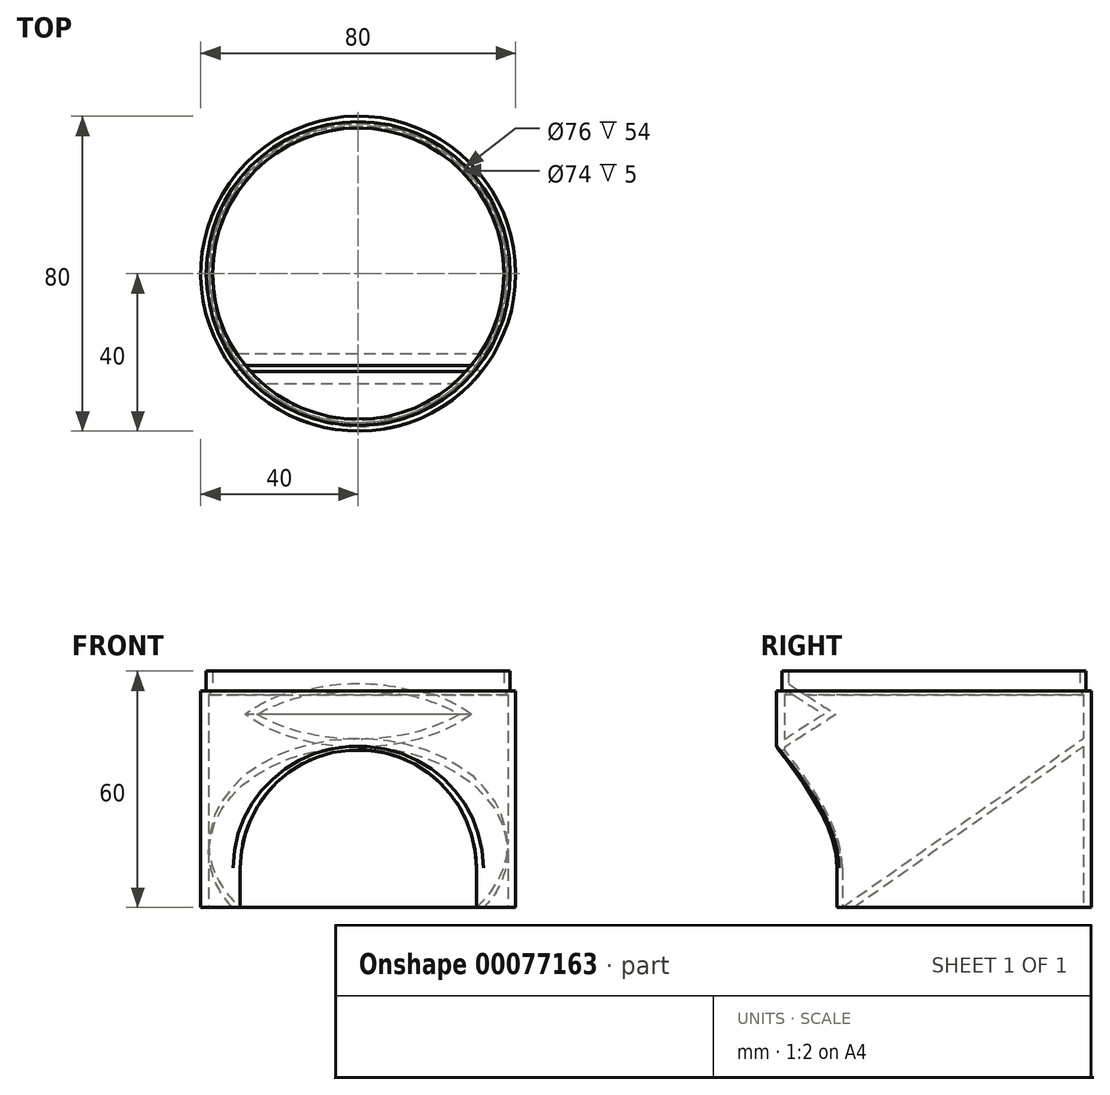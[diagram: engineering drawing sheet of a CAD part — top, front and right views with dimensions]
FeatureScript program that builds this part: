
annotation { "Feature Type Name" : "Feature", "Feature Type Description" : "" }
export const myFeature = defineFeature(function(context is Context, id is Id, definition is map)
    precondition{}
    {
        {
            var Q0;
            Q0=qCreatedBy(makeId("Top.planeOp"),FACE);
            var sketch = newSketch(context, id + "F0", { "sketchPlane" : qUnion([Q0])});
            skCircle(sketch, "E0", {"center": v(0, 0) * mm, "radius": 40 * mm});
            skCircle(sketch, "E1", {"center": v(0, 0) * mm, "radius": 38 * mm});
            skLineSegment(sketch, "E2", {"start": v(38, 0) * mm, "end": v(40, 0) * mm});
            skSolve(sketch);
        }
        {
            var Q0;
            Q0=qSketchRegion(id+"F0",true);
            extrude(context, id + "F1", {"entities" : qUnion([Q0]), "depth" : 60 * mm});
        }
        {
            var Q0;
            Q0=qCreatedBy(makeId("Front.planeOp"),FACE);
            var sketch = newSketch(context, id + "F2", { "sketchPlane" : qUnion([Q0])});
            skLineSegment(sketch, "E3", {"start": v(0, 0) * mm, "end": v(0, 60) * mm, "construction": true});
            skLineSegment(sketch, "E4", {"start": v(0, 60) * mm, "end": v(38.6, 60) * mm, "construction": true});
            skLineSegment(sketch, "E5", {"start": v(38.6, 60) * mm, "end": v(38.6, 55) * mm});
            skLineSegment(sketch, "E6", {"start": v(38.6, 55) * mm, "end": v(40, 55) * mm});
            skLineSegment(sketch, "E7", {"start": v(40, 55) * mm, "end": v(40, 60) * mm});
            skLineSegment(sketch, "E8", {"start": v(40, 60) * mm, "end": v(38.6, 60) * mm});
            skSolve(sketch);
        }
        {
            var Q0;
            Q0=qSketchRegion(id+"F2",true);
            var Q1;
            Q1=sQuery(id+"F2.wireOp",EDGE,"E3");
            revolve(context, id + "F3", {"operationType" : NewBodyOperationType.REMOVE, "entities" : qUnion([Q0]), "axis" : qUnion([Q1]), "revolveType" : RevolveType.FULL, "oppositeDirection" : true});
        }
        {
            var Q0;
            Q0=qCreatedBy(makeId("Right.planeOp"),FACE);
            var sketch = newSketch(context, id + "F4", { "sketchPlane" : qUnion([Q0])});
            skLineSegment(sketch, "E9", {"start": v(-9, 32) * mm, "end": v(9, 32) * mm, "construction": true});
            skLineSegment(sketch, "E10", {"start": v(-24.86, 41) * mm, "end": v(-24.86, 49) * mm, "construction": true});
            skLineSegment(sketch, "E11", {"start": v(-24.86, 49) * mm, "end": v(-38, 57.37) * mm});
            skLineSegment(sketch, "E12", {"start": v(-38, 57.37) * mm, "end": v(-38, 55.37) * mm});
            skLineSegment(sketch, "E13", {"start": v(-38, 55.37) * mm, "end": v(-28, 49) * mm});
            skLineSegment(sketch, "E14", {"start": v(-28, 49) * mm, "end": v(-38, 42.63) * mm});
            skLineSegment(sketch, "E15", {"start": v(-24.86, 49) * mm, "end": v(-38, 40.63) * mm});
            skLineSegment(sketch, "E16", {"start": v(-38, 40.63) * mm, "end": v(-38, 42.63) * mm});
            skLineSegment(sketch, "E17", {"start": v(-38, 55.37) * mm, "end": v(-38, 40.63) * mm, "construction": true});
            skLineSegment(sketch, "E18", {"start": v(-28, 49) * mm, "end": v(-24.86, 49) * mm, "construction": true});
            skLineSegment(sketch, "E19", {"start": v(0, 0) * mm, "end": v(0, 32) * mm, "construction": true});
            skLineSegment(sketch, "E20", {"start": v(0, 0) * mm, "end": v(-23.3, 0) * mm, "construction": true});
            skLineSegment(sketch, "E21", {"start": v(9, 32) * mm, "end": v(38, 32) * mm, "construction": true});
            skLineSegment(sketch, "E22", {"start": v(38, 42.92) * mm, "end": v(38, 40.92) * mm});
            skLineSegment(sketch, "E23", {"start": v(38, 40.92) * mm, "end": v(-20.44, 0) * mm});
            skLineSegment(sketch, "E24", {"start": v(-23.3, 0) * mm, "end": v(-20.44, 0) * mm});
            skLineSegment(sketch, "E25", {"start": v(38, 32) * mm, "end": v(38, 32) * mm});
            skLineSegment(sketch, "E26", {"start": v(-23.3, 0) * mm, "end": v(38, 42.92) * mm});
            skLineSegment(sketch, "E27", {"start": v(-28, 49) * mm, "end": v(-38, 49) * mm, "construction": true});
            skLineSegment(sketch, "E28.MirrorCS", {"start": v(-9, 32) * mm, "end": v(-38, 32) * mm});
            skLineSegment(sketch, "E29", {"start": v(-38, 32) * mm, "end": v(-38, 49) * mm, "construction": true});
            skSolve(sketch);
        }
        {
            var Q0;
            Q0=makeQuery(id+"F4.imprint","IMPRINT",FACE,{"disambiguationData":[TD([[makeQuery(id+"F4.imprint","IMPRINT",EDGE,{"derivedFrom":sQuery(id+"F4.wireOp",EDGE,"E11")}),1.0]])]});
            var Q1;
            Q1=makeQuery(id+"F4.imprint","IMPRINT",FACE,{"disambiguationData":[TD([[makeQuery(id+"F4.imprint","IMPRINT",EDGE,{"derivedFrom":sQuery(id+"F4.wireOp",EDGE,"E22")}),-1.0]])]});
            extrude(context, id + "F5", {"entities" : qUnion([Q0, Q1]), "operationType" : NewBodyOperationType.ADD, "endBound" : BoundingType.UP_TO_NEXT, "depth" : 25 * mm, "hasSecondDirection" : true, "secondDirectionBound" : SecondDirectionBoundingType.UP_TO_NEXT, "secondDirectionOppositeDirection" : true, "secondDirectionDepth" : 25 * mm});
        }
        {
            var Q0;
            Q0=qCreatedBy(makeId("Front.planeOp"),FACE);
            cPlane(context, id + "F6", {"entities" : qUnion([Q0]), "cplaneType" : CPlaneType.OFFSET, "offset" : 23.3 * mm, "width" : 150 * mm, "height" : 150 * mm});
        }
        {
            var Q0;
            Q0=qCreatedBy(id+"F6.planeOp",FACE);
            var sketch = newSketch(context, id + "F7", { "sketchPlane" : qUnion([Q0])});
            skLineSegment(sketch, "E30", {"start": v(-30, 0) * mm, "end": v(30, 0) * mm});
            skLineSegment(sketch, "E31", {"start": v(-30, 0) * mm, "end": v(-30, 10) * mm});
            skLineSegment(sketch, "E32", {"start": v(30, 0) * mm, "end": v(30, 10) * mm});
            skArc(sketch, "E33", {"start": v(30, 10) * mm, "mid": v(0, 40) * mm, "end": v(-30, 10) * mm});
            skSolve(sketch);
        }
        {
            var Q0;
            Q0=qSketchRegion(id+"F7",true);
            extrude(context, id + "F8", {"entities" : qUnion([Q0]), "operationType" : NewBodyOperationType.REMOVE, "endBound" : BoundingType.THROUGH_ALL, "depth" : 25 * mm});
        }
        {
            var Q0;
            Q0=makeQuery(id+"F8.boolean.opBoolean","INTERSECT",EDGE,{"derivedFrom":[makeQuery(id+"F1.opExtrude","SWEPT_FACE",FACE,{"disambiguationData":[OSD([sQuery(id+"F0.wireOp",EDGE,"E0")])]}),makeQuery(id+"F8.opExtrude","SWEPT_FACE",FACE,{"disambiguationData":[OSD([sQuery(id+"F7.wireOp",EDGE,"E31")])]})]});
            fillet(context, id + "F9", {"entities" : qUnion([Q0]), "radius" : 1 * mm, "tangentPropagation" : true, "allowEdgeOverflow" : false});
        }
        {
            var Q0;
            Q0=qCreatedBy(makeId("Front.planeOp"),FACE);
            var sketch = newSketch(context, id + "F10", { "sketchPlane" : qUnion([Q0])});
            skLineSegment(sketch, "E34", {"start": v(0, 0) * mm, "end": v(0, 60) * mm, "construction": true});
            skLineSegment(sketch, "E35.0", {"start": v(-38, 60) * mm, "end": v(38, 60) * mm, "construction": true});
            skLineSegment(sketch, "E36.bottom", {"start": v(38, 60) * mm, "end": v(37, 60) * mm});
            skLineSegment(sketch, "E36.left", {"start": v(38, 60) * mm, "end": v(38, 54) * mm});
            skLineSegment(sketch, "E36.right", {"start": v(37, 60) * mm, "end": v(37, 55) * mm});
            skLineSegment(sketch, "E37", {"start": v(37, 55) * mm, "end": v(38, 54) * mm});
            skSolve(sketch);
        }
        {
            var Q0;
            Q0=qSketchRegion(id+"F10",true);
            var Q1;
            Q1=sQuery(id+"F10.wireOp",EDGE,"E34");
            revolve(context, id + "F11", {"operationType" : NewBodyOperationType.ADD, "entities" : qUnion([Q0]), "axis" : qUnion([Q1]), "revolveType" : RevolveType.FULL});
        }
    });
